# Revit family: EKF_EE_ВертикальныйП-образныйПрофиль_PROxima
name_source: partatom
category: Электрооборудование
units: mm (PartAtom-declared; Revit-internal decimal feet)

## family parameters
Всегда вертикально = Нет
На основе рабочей плоскости = Да
Общий = Да
При загрузке вырезать с полостями = Нет
Размер круглого соединителя = Использовать диаметр
Тип детали = Силовой щит
Точка расчета площади = Нет

## types (2) — shared parameters
ADSK_Единица измерения = шт.
ADSK_Завод-изготовитель = EKF
ADSK_Количество = 1
ADSK_Марка = Вертикальный П-образный профиль
ADSK_Материал = Сталь_Оцинкованная
ADSK_Обозначение = Вертикальный П-образный профиль
ADSK_Размер_Глубина = 40 мм
ADSK_Размер_Ширина = 40 мм
a = 40 мм
t = 1.2 мм
Изготовитель = EKF
Отметка по умолчанию = 1219.2 мм
Серия номенклатуры = Unit PROxima
Степень защиты IP = -
ТВ = EKF_2
Тип установки = -
Шаг = 35 мм
zero-valued in all types: ADSK_Масса

## per-type parameters (varying)
| type | ADSK_Код изделия | ADSK_Наименование | ADSK_Размер_Высота | Отступ | Тип |
| Вертикальный П-образный профиль для ВРУ Unit и ЩО-70 (2000хШхГ) EKF PROxima | mb15-04-05p | Вертикальный П-образный профиль для ВРУ Unit и ЩО-70  (2000хШхГ) EKF PROxima | 1800 мм | 25 мм | 11 мм |
| Вертикальный П-образный профиль для ВРУ Unit и ЩО-70 (1800хШхГ) EKF PROxima | mb15-07-02p | Вертикальный П-образный профиль для ВРУ Unit и ЩО-70 (1800хШхГ) EKF PROxima | 1600 мм | 30 мм | 12 мм |
